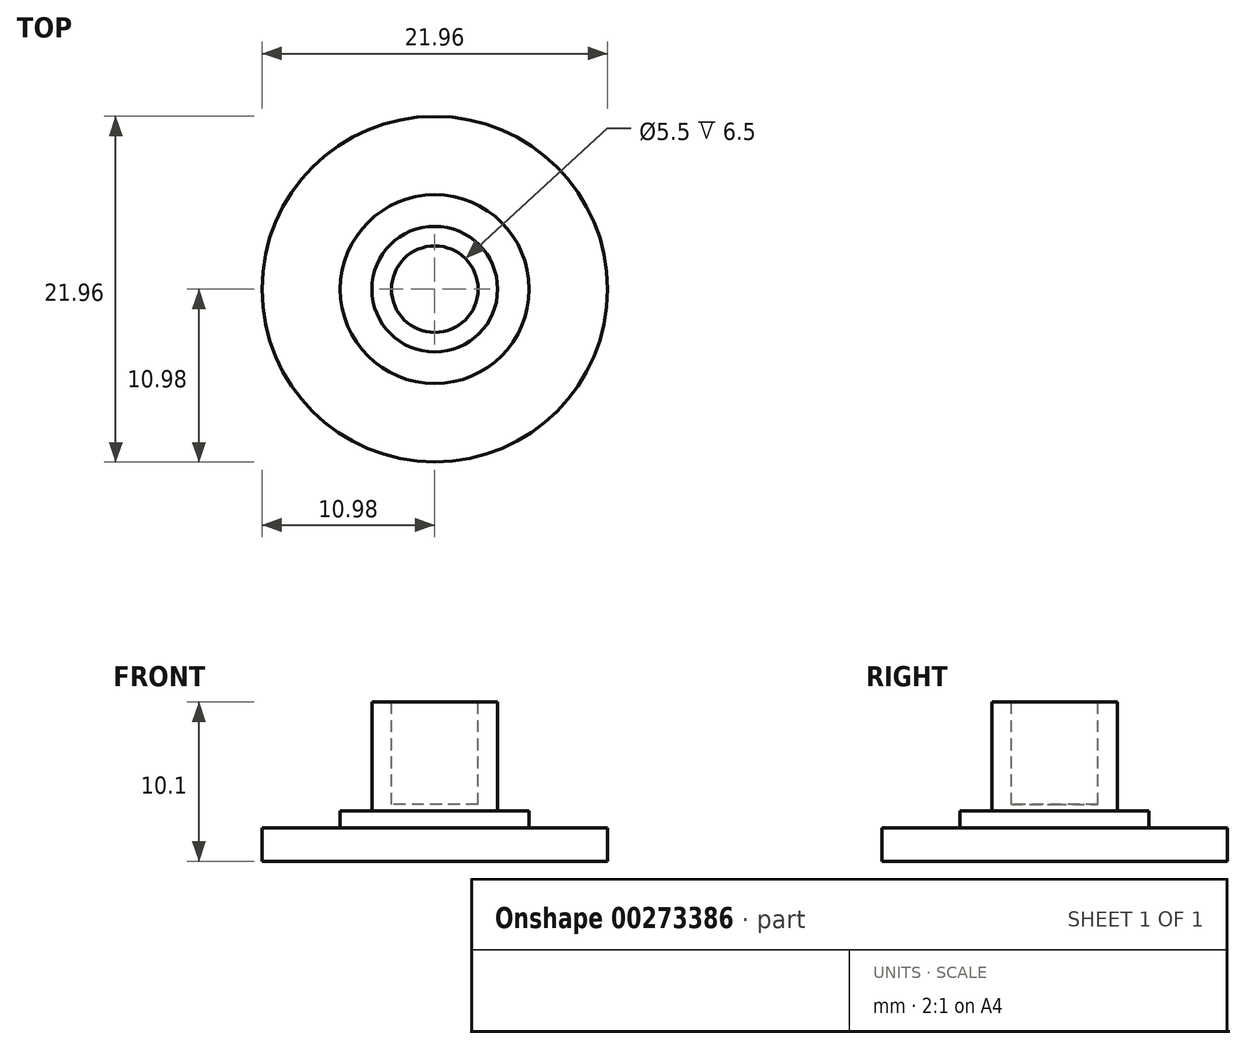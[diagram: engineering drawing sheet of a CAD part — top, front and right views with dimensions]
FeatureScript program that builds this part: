
annotation { "Feature Type Name" : "Feature", "Feature Type Description" : "" }
export const myFeature = defineFeature(function(context is Context, id is Id, definition is map)
    precondition{}
    {
        {
            var Q0;
            Q0=qCreatedBy(makeId("Top.planeOp"),FACE);
            var sketch = newSketch(context, id + "F0", { "sketchPlane" : qUnion([Q0])});
            skCircle(sketch, "E0", {"center": v(0, 0) * mm, "radius": 10.97 * mm});
            skSolve(sketch);
        }
        {
            var Q0;
            Q0=makeQuery(id+"F0.imprint","IMPRINT",FACE,{"disambiguationData":[TD([[makeQuery(id+"F0.imprint","IMPRINT",EDGE,{"derivedFrom":sQuery(id+"F0.wireOp",EDGE,"E0")}),1.0]])]});
            extrude(context, id + "F1", {"entities" : qUnion([Q0]), "depth" : 2.1 * mm});
        }
        {
            var Q0;
            Q0=makeQuery(id+"F1.opExtrude","CAP_FACE",FACE,{"disambiguationData":[OSD([sQuery(id+"F0.wireOp",EDGE,"E0")])],"isStart":false});
            var sketch = newSketch(context, id + "F2", { "sketchPlane" : qUnion([Q0])});
            skCircle(sketch, "E1", {"center": v(0, 0) * mm, "radius": 6 * mm});
            skSolve(sketch);
        }
        {
            var Q0;
            Q0=makeQuery(id+"F2.imprint","IMPRINT",FACE,{"disambiguationData":[TD([[makeQuery(id+"F2.imprint","IMPRINT",EDGE,{"derivedFrom":sQuery(id+"F2.wireOp",EDGE,"E1")}),1.0]])]});
            extrude(context, id + "F3", {"entities" : qUnion([Q0]), "depth" : 1.1 * mm});
        }
        {
            var Q0;
            Q0=makeQuery(id+"F3.opExtrude","CAP_FACE",FACE,{"disambiguationData":[OSD([sQuery(id+"F2.wireOp",EDGE,"E1")])],"isStart":false});
            var sketch = newSketch(context, id + "F4", { "sketchPlane" : qUnion([Q0])});
            skCircle(sketch, "E2", {"center": v(0, 0) * mm, "radius": 4 * mm});
            skSolve(sketch);
        }
        {
            var Q0;
            Q0=makeQuery(id+"F4.imprint","IMPRINT",FACE,{"disambiguationData":[TD([[makeQuery(id+"F4.imprint","IMPRINT",EDGE,{"derivedFrom":sQuery(id+"F4.wireOp",EDGE,"E2")}),1.0]])]});
            extrude(context, id + "F5", {"entities" : qUnion([Q0]), "operationType" : NewBodyOperationType.ADD, "depth" : 6.9 * mm});
        }
        {
            var Q0;
            Q0=makeQuery(id+"F5.opExtrude","CAP_FACE",FACE,{"disambiguationData":[OSD([sQuery(id+"F4.wireOp",EDGE,"E2")])],"isStart":false});
            var sketch = newSketch(context, id + "F6", { "sketchPlane" : qUnion([Q0])});
            skCircle(sketch, "E3", {"center": v(0, 0) * mm, "radius": 2.75 * mm});
            skSolve(sketch);
        }
        {
            var Q0;
            Q0=makeQuery(id+"F6.imprint","IMPRINT",FACE,{"disambiguationData":[TD([[makeQuery(id+"F6.imprint","IMPRINT",EDGE,{"derivedFrom":sQuery(id+"F6.wireOp",EDGE,"E3")}),1.0]])]});
            extrude(context, id + "F7", {"entities" : qUnion([Q0]), "operationType" : NewBodyOperationType.REMOVE, "oppositeDirection" : true, "depth" : 6.5 * mm});
        }
    });
